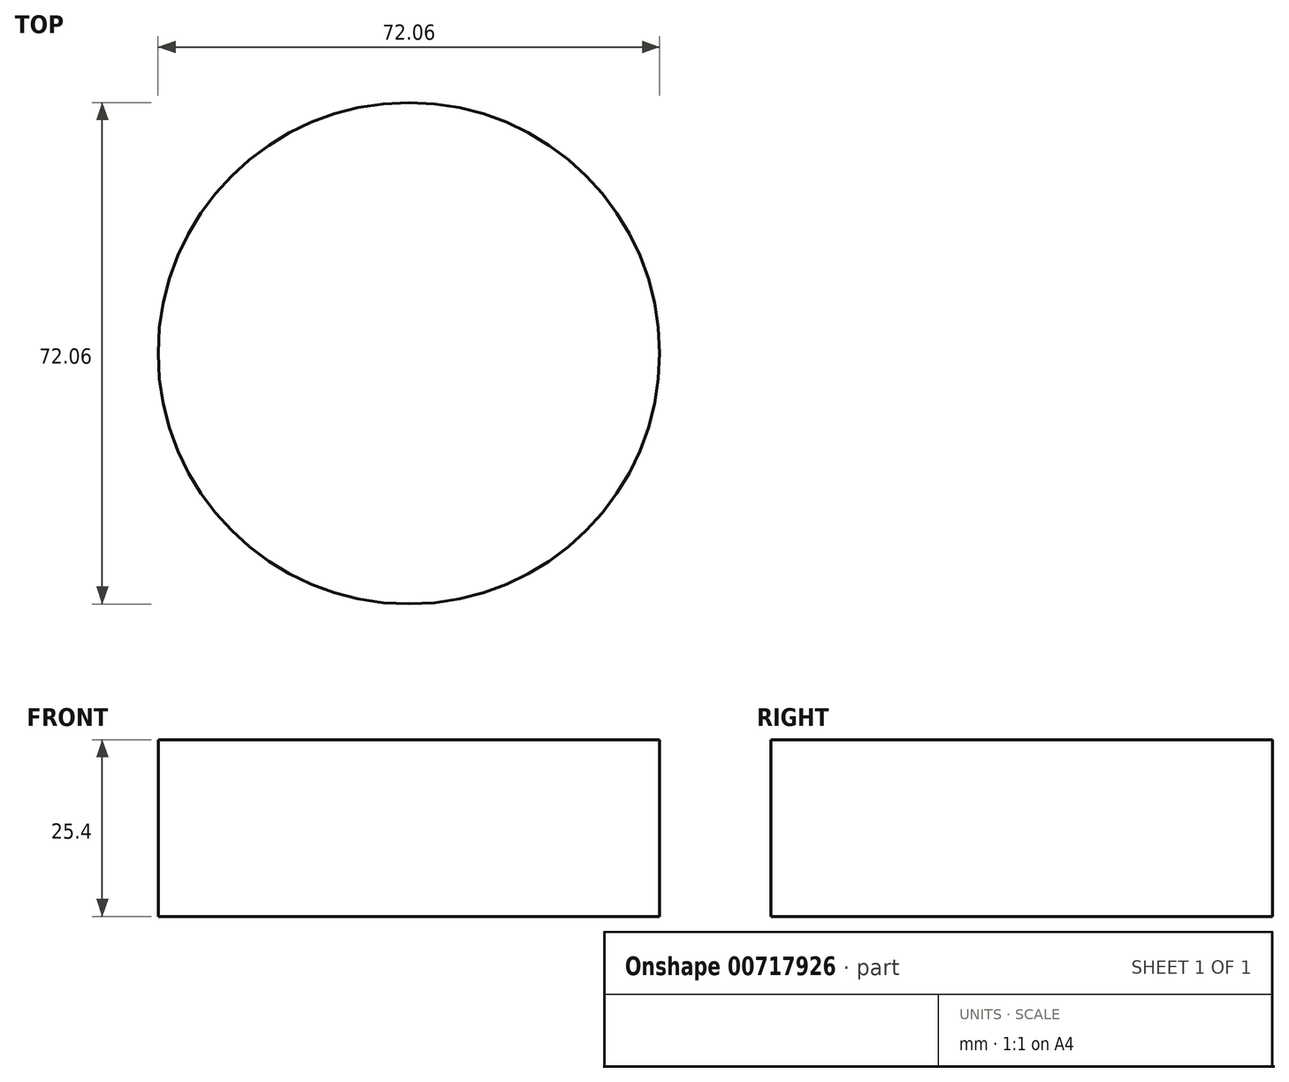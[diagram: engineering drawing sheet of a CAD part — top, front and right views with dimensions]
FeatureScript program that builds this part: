
annotation { "Feature Type Name" : "Feature", "Feature Type Description" : "" }
export const myFeature = defineFeature(function(context is Context, id is Id, definition is map)
    precondition{}
    {
        {
            var Q0;
            Q0=qCreatedBy(makeId("Top.planeOp"),FACE);
            var sketch = newSketch(context, id + "F0", { "sketchPlane" : qUnion([Q0])});
            skCircle(sketch, "E0", {"center": v(0, 0) * mm, "radius": 36.03 * mm});
            skSolve(sketch);
        }
        {
            var Q0;
            Q0=makeQuery(id+"F0.imprint","IMPRINT",FACE,{"disambiguationData":[TD([[makeQuery(id+"F0.imprint","IMPRINT",EDGE,{"derivedFrom":sQuery(id+"F0.wireOp",EDGE,"E0")}),1.0]])]});
            extrude(context, id + "F1", {"entities" : qUnion([Q0]), "depth" : 25.4 * mm, "offsetDistance" : 25.4 * mm});
        }
    });
